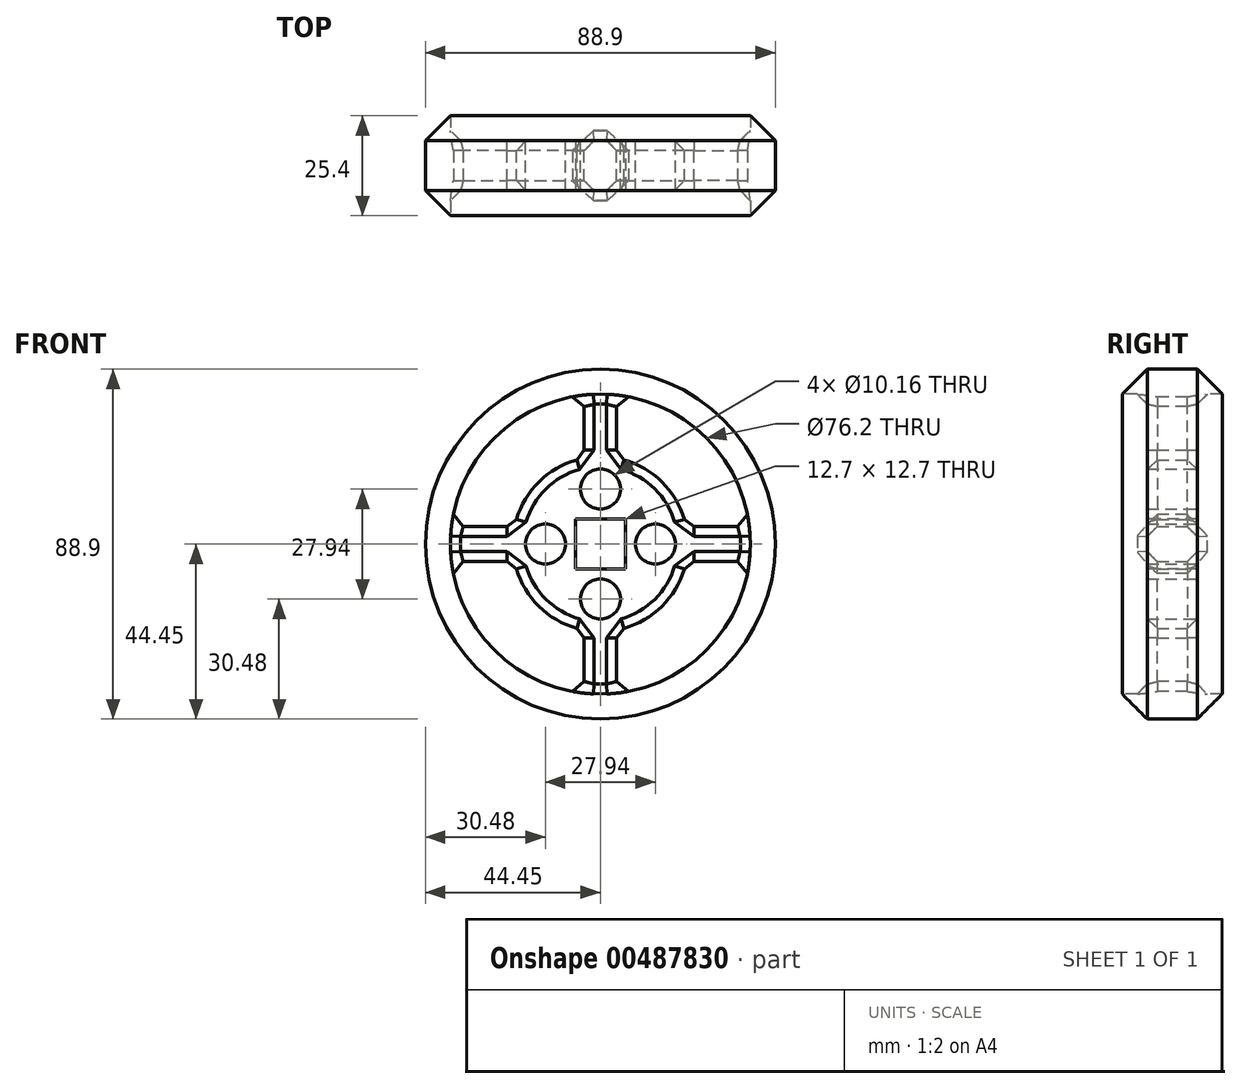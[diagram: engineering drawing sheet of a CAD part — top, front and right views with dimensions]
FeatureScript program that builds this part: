
annotation { "Feature Type Name" : "Feature", "Feature Type Description" : "" }
export const myFeature = defineFeature(function(context is Context, id is Id, definition is map)
    precondition{}
    {
        {
            var Q0;
            Q0=qCreatedBy(makeId("Front.planeOp"),FACE);
            var sketch = newSketch(context, id + "F0", { "sketchPlane" : qUnion([Q0])});
            skCircle(sketch, "E0", {"center": v(0, 0) * mm, "radius": 44.45 * mm});
            skSolve(sketch);
        }
        {
            var Q0;
            Q0=makeQuery(id+"F0.imprint","IMPRINT",FACE,{"disambiguationData":[TD([[makeQuery(id+"F0.imprint","IMPRINT",EDGE,{"derivedFrom":sQuery(id+"F0.wireOp",EDGE,"E0")}),1.0]])]});
            extrude(context, id + "F1", {"entities" : qUnion([Q0]), "depth" : 12.7 * mm});
        }
        {
            var Q0;
            Q0=makeQuery(id+"F1.opExtrude","CAP_FACE",FACE,{"disambiguationData":[OSD([sQuery(id+"F0.wireOp",EDGE,"E0")])],"isStart":false});
            var sketch = newSketch(context, id + "F2", { "sketchPlane" : qUnion([Q0])});
            skCircle(sketch, "E1", {"center": v(0, 0) * mm, "radius": 50.8 * mm});
            skSolve(sketch);
        }
        {
            var Q0;
            Q0=sQuery(id+"F2.wireOp",VERTEX,"E1.center");
            var Q1;
            Q1=makeQuery(id+"F1.opExtrude","SWEPT_BODY",BODY,{"disambiguationData":[OSD([sQuery(id+"F0.wireOp",EDGE,"E0")])]});
            hole(context, id + "F3", {"style" : HoleStyle.SIMPLE, "endStyle" : HoleEndStyle.THROUGH, "holeDiameter" : 76.2 * mm, "isTappedThrough" : true, "tappedDepth" : 12.7 * mm, "tapClearance" : 3, "locations" : qUnion([Q0]), "scope" : qUnion([Q1])});
        }
        {
            var Q0;
            Q0=qCreatedBy(makeId("Front.planeOp"),FACE);
            var sketch = newSketch(context, id + "F4", { "sketchPlane" : qUnion([Q0])});
            skLineSegment(sketch, "E2.bottom", {"start": v(4.13, -42.15) * mm, "end": v(-4.13, -42.15) * mm});
            skLineSegment(sketch, "E2.top", {"start": v(4.13, 42.15) * mm, "end": v(-4.13, 42.15) * mm});
            skLineSegment(sketch, "E2.left", {"start": v(4.13, -42.15) * mm, "end": v(4.13, 42.15) * mm});
            skLineSegment(sketch, "E2.right", {"start": v(-4.13, -42.15) * mm, "end": v(-4.13, 42.15) * mm});
            skPoint(sketch, "E2.middle", {"position": v(0, 0) * mm});
            skLineSegment(sketch, "E3.bottom", {"start": v(42.66, 4.46) * mm, "end": v(-42.66, 4.46) * mm});
            skLineSegment(sketch, "E3.top", {"start": v(42.66, -4.46) * mm, "end": v(-42.66, -4.46) * mm});
            skLineSegment(sketch, "E3.left", {"start": v(42.66, 4.46) * mm, "end": v(42.66, -4.46) * mm});
            skLineSegment(sketch, "E3.right", {"start": v(-42.66, 4.46) * mm, "end": v(-42.66, -4.46) * mm});
            skSolve(sketch);
        }
        {
            var Q0;
            {var subQ5=sQuery(id+"F4.wireOp",EDGE,"E3.left");Q0=makeQuery(id+"F4.imprint","IMPRINT",FACE,{"disambiguationData":[TD([[makeQuery(id+"F4.imprint","IMPRINT",EDGE,{"derivedFrom":subQ5}),-1.0]])]});}
            var Q1;
            {var subQ5=sQuery(id+"F4.wireOp",EDGE,"E3.right");Q1=makeQuery(id+"F4.imprint","IMPRINT",FACE,{"disambiguationData":[TD([[makeQuery(id+"F4.imprint","IMPRINT",EDGE,{"derivedFrom":subQ5}),1.0]])]});}
            var Q2;
            {var subQ0=sQuery(id+"F4.wireOp",EDGE,"E3.top");var subQ1=sQuery(id+"F4.wireOp",EDGE,"E2.left");var subQ2=makeQuery(id+"F4.imprint","INTERSECT",VERTEX,{"derivedFrom":[subQ1,subQ0]});Q2=makeQuery(id+"F4.imprint","IMPRINT",FACE,{"disambiguationData":[TD([[makeQuery(id+"F4.imprint","IMPRINT",EDGE,{"disambiguationData":[TD([[subQ2,-1.0]])],"derivedFrom":subQ1}),1.0]])]});}
            var Q3;
            {var subQ0=sQuery(id+"F4.wireOp",EDGE,"E2.top");Q3=makeQuery(id+"F4.imprint","IMPRINT",FACE,{"disambiguationData":[TD([[makeQuery(id+"F4.imprint","IMPRINT",EDGE,{"derivedFrom":subQ0}),1.0]])]});}
            var Q4;
            {var subQ0=sQuery(id+"F4.wireOp",EDGE,"E2.bottom");Q4=makeQuery(id+"F4.imprint","IMPRINT",FACE,{"disambiguationData":[TD([[makeQuery(id+"F4.imprint","IMPRINT",EDGE,{"derivedFrom":subQ0}),-1.0]])]});}
            extrude(context, id + "F5", {"entities" : qUnion([Q0, Q1, Q2, Q3, Q4]), "operationType" : NewBodyOperationType.ADD, "depth" : 6.35 * mm});
        }
        {
            var Q0;
            Q0=qCreatedBy(makeId("Front.planeOp"),FACE);
            var sketch = newSketch(context, id + "F6", { "sketchPlane" : qUnion([Q0])});
            skCircle(sketch, "E4", {"center": v(0, 0) * mm, "radius": 22.23 * mm});
            skSolve(sketch);
        }
        {
            var Q0;
            Q0=makeQuery(id+"F6.imprint","IMPRINT",FACE,{"disambiguationData":[TD([[makeQuery(id+"F6.imprint","IMPRINT",EDGE,{"derivedFrom":sQuery(id+"F6.wireOp",EDGE,"E4")}),1.0]])]});
            extrude(context, id + "F7", {"entities" : qUnion([Q0]), "operationType" : NewBodyOperationType.ADD, "depth" : 6.35 * mm});
        }
        {
            var Q0;
            Q0=qCreatedBy(makeId("Front.planeOp"),FACE);
            var sketch = newSketch(context, id + "F8", { "sketchPlane" : qUnion([Q0])});
            skCircle(sketch, "E5", {"center": v(0, 13.97) * mm, "radius": 5.08 * mm});
            skCircle(sketch, "E6", {"center": v(13.97, 0) * mm, "radius": 5.08 * mm});
            skCircle(sketch, "E7", {"center": v(0, -13.97) * mm, "radius": 5.08 * mm});
            skCircle(sketch, "E8", {"center": v(-13.97, 0) * mm, "radius": 5.08 * mm});
            skSolve(sketch);
        }
        {
            var Q0;
            Q0=qSketchRegion(id+"F8",true);
            extrude(context, id + "F9", {"entities" : qUnion([Q0]), "operationType" : NewBodyOperationType.REMOVE, "endBound" : BoundingType.THROUGH_ALL, "depth" : 25.4 * mm});
        }
        {
            var Q0;
            Q0=makeQuery(id+"F1.opExtrude","SWEPT_BODY",BODY,{"disambiguationData":[OSD([sQuery(id+"F0.wireOp",EDGE,"E0")])]});
            var Q1;
            Q1=qCreatedBy(makeId("Front.planeOp"),FACE);
            mirror(context, id + "F10", {"operationType" : NewBodyOperationType.ADD, "entities" : qUnion([Q0]), "mirrorPlane" : qUnion([Q1])});
        }
        {
            var Q0;
            {var subQ0=makeQuery(id+"F1.opExtrude","SWEPT_FACE",FACE,{"disambiguationData":[OSD([sQuery(id+"F0.wireOp",EDGE,"E0")])]});Q0=makeQuery(id+"F10.boolean.opBoolean","MERGE",FACE,{"derivedFrom":[subQ0,makeQuery(id+"F10.opPattern","COPY",FACE,{"derivedFrom":subQ0,"instanceName":"1"})]});}
            chamfer(context, id + "F11", {"entities" : qUnion([Q0]), "width" : 6.35 * mm, "tangentPropagation" : true});
        }
        {
            var Q0;
            {var subQ0=sQuery(id+"F4.wireOp",EDGE,"E3.top");var subQ1=makeQuery(id+"F5.opExtrude","SWEPT_FACE",FACE,{"disambiguationData":[OSD([subQ0]),TDD([makeQuery(id+"F4.imprint","IMPRINT",EDGE,{"disambiguationData":[TD([[makeQuery(id+"F4.imprint","INTERSECT",VERTEX,{"derivedFrom":[subQ0,sQuery(id+"F4.wireOp",EDGE,"E3.right")]}),1.0]])],"derivedFrom":subQ0})])]});Q0=makeQuery(id+"F10.boolean.opBoolean","MERGE",FACE,{"derivedFrom":[subQ1,makeQuery(id+"F10.opPattern","COPY",FACE,{"derivedFrom":subQ1,"instanceName":"1"})]});}
            var Q1;
            {var subQ0=sQuery(id+"F4.wireOp",EDGE,"E3.bottom");var subQ1=makeQuery(id+"F5.opExtrude","SWEPT_FACE",FACE,{"disambiguationData":[OSD([subQ0]),TDD([makeQuery(id+"F4.imprint","IMPRINT",EDGE,{"disambiguationData":[TD([[makeQuery(id+"F4.imprint","INTERSECT",VERTEX,{"derivedFrom":[subQ0,sQuery(id+"F4.wireOp",EDGE,"E3.right")]}),1.0]])],"derivedFrom":subQ0})])]});Q1=makeQuery(id+"F10.boolean.opBoolean","MERGE",FACE,{"derivedFrom":[subQ1,makeQuery(id+"F10.opPattern","COPY",FACE,{"derivedFrom":subQ1,"instanceName":"1"})]});}
            var Q2;
            {var subQ0=sQuery(id+"F4.wireOp",EDGE,"E2.right");var subQ1=makeQuery(id+"F5.opExtrude","SWEPT_FACE",FACE,{"disambiguationData":[OSD([subQ0]),TDD([makeQuery(id+"F4.imprint","IMPRINT",EDGE,{"disambiguationData":[TD([[makeQuery(id+"F4.imprint","INTERSECT",VERTEX,{"derivedFrom":[sQuery(id+"F4.wireOp",EDGE,"E2.top"),subQ0]}),1.0]])],"derivedFrom":subQ0})])]});Q2=makeQuery(id+"F10.boolean.opBoolean","MERGE",FACE,{"derivedFrom":[subQ1,makeQuery(id+"F10.opPattern","COPY",FACE,{"derivedFrom":subQ1,"instanceName":"1"})]});}
            var Q3;
            {var subQ0=sQuery(id+"F4.wireOp",EDGE,"E2.left");var subQ1=makeQuery(id+"F5.opExtrude","SWEPT_FACE",FACE,{"disambiguationData":[OSD([subQ0]),TDD([makeQuery(id+"F4.imprint","IMPRINT",EDGE,{"disambiguationData":[TD([[makeQuery(id+"F4.imprint","INTERSECT",VERTEX,{"derivedFrom":[sQuery(id+"F4.wireOp",EDGE,"E2.top"),subQ0]}),1.0]])],"derivedFrom":subQ0})])]});Q3=makeQuery(id+"F10.boolean.opBoolean","MERGE",FACE,{"derivedFrom":[subQ1,makeQuery(id+"F10.opPattern","COPY",FACE,{"derivedFrom":subQ1,"instanceName":"1"})]});}
            var Q4;
            {var subQ0=sQuery(id+"F4.wireOp",EDGE,"E3.bottom");var subQ1=makeQuery(id+"F5.opExtrude","SWEPT_FACE",FACE,{"disambiguationData":[OSD([subQ0]),TDD([makeQuery(id+"F4.imprint","IMPRINT",EDGE,{"disambiguationData":[TD([[makeQuery(id+"F4.imprint","INTERSECT",VERTEX,{"derivedFrom":[subQ0,sQuery(id+"F4.wireOp",EDGE,"E3.left")]}),-1.0]])],"derivedFrom":subQ0})])]});Q4=makeQuery(id+"F10.boolean.opBoolean","MERGE",FACE,{"derivedFrom":[subQ1,makeQuery(id+"F10.opPattern","COPY",FACE,{"derivedFrom":subQ1,"instanceName":"1"})]});}
            var Q5;
            {var subQ0=sQuery(id+"F4.wireOp",EDGE,"E3.top");var subQ1=makeQuery(id+"F5.opExtrude","SWEPT_FACE",FACE,{"disambiguationData":[OSD([subQ0]),TDD([makeQuery(id+"F4.imprint","IMPRINT",EDGE,{"disambiguationData":[TD([[makeQuery(id+"F4.imprint","INTERSECT",VERTEX,{"derivedFrom":[subQ0,sQuery(id+"F4.wireOp",EDGE,"E3.left")]}),-1.0]])],"derivedFrom":subQ0})])]});Q5=makeQuery(id+"F10.boolean.opBoolean","MERGE",FACE,{"derivedFrom":[subQ1,makeQuery(id+"F10.opPattern","COPY",FACE,{"derivedFrom":subQ1,"instanceName":"1"})]});}
            var Q6;
            {var subQ0=sQuery(id+"F4.wireOp",EDGE,"E2.left");var subQ1=makeQuery(id+"F5.opExtrude","SWEPT_FACE",FACE,{"disambiguationData":[OSD([subQ0]),TDD([makeQuery(id+"F4.imprint","IMPRINT",EDGE,{"disambiguationData":[TD([[makeQuery(id+"F4.imprint","INTERSECT",VERTEX,{"derivedFrom":[sQuery(id+"F4.wireOp",EDGE,"E2.bottom"),subQ0]}),-1.0]])],"derivedFrom":subQ0})])]});Q6=makeQuery(id+"F10.boolean.opBoolean","MERGE",FACE,{"derivedFrom":[subQ1,makeQuery(id+"F10.opPattern","COPY",FACE,{"derivedFrom":subQ1,"instanceName":"1"})]});}
            var Q7;
            {var subQ0=sQuery(id+"F4.wireOp",EDGE,"E2.right");var subQ1=makeQuery(id+"F5.opExtrude","SWEPT_FACE",FACE,{"disambiguationData":[OSD([subQ0]),TDD([makeQuery(id+"F4.imprint","IMPRINT",EDGE,{"disambiguationData":[TD([[makeQuery(id+"F4.imprint","INTERSECT",VERTEX,{"derivedFrom":[sQuery(id+"F4.wireOp",EDGE,"E2.bottom"),subQ0]}),-1.0]])],"derivedFrom":subQ0})])]});Q7=makeQuery(id+"F10.boolean.opBoolean","MERGE",FACE,{"derivedFrom":[subQ1,makeQuery(id+"F10.opPattern","COPY",FACE,{"derivedFrom":subQ1,"instanceName":"1"})]});}
            var Q8;
            {var subQ4=sQuery(id+"F4.wireOp",EDGE,"E2.right");var subQ7=sQuery(id+"F4.wireOp",EDGE,"E2.bottom");var subQ9=sQuery(id+"F6.wireOp",EDGE,"E4");var subQ10=makeQuery(id+"F7.boolean.opBoolean","SPLIT",FACE,{"disambiguationData":[TD([makeQuery(id+"F5.opExtrude","SWEPT_FACE",FACE,{"disambiguationData":[OSD([subQ4]),TDD([makeQuery(id+"F4.imprint","IMPRINT",EDGE,{"disambiguationData":[TD([[makeQuery(id+"F4.imprint","INTERSECT",VERTEX,{"derivedFrom":[subQ7,subQ4]}),-1.0]])],"derivedFrom":subQ4})])]})])],"derivedFrom":makeQuery(id+"F7.opExtrude","SWEPT_FACE",FACE,{"disambiguationData":[OSD([subQ9])]})});Q8=makeQuery(id+"F10.boolean.opBoolean","MERGE",FACE,{"derivedFrom":[subQ10,makeQuery(id+"F10.opPattern","COPY",FACE,{"derivedFrom":subQ10,"instanceName":"1"})]});}
            var Q9;
            {var subQ0=sQuery(id+"F4.wireOp",EDGE,"E2.right");var subQ1=sQuery(id+"F4.wireOp",EDGE,"E2.top");var subQ4=sQuery(id+"F6.wireOp",EDGE,"E4");var subQ10=makeQuery(id+"F7.boolean.opBoolean","SPLIT",FACE,{"disambiguationData":[TD([makeQuery(id+"F5.opExtrude","SWEPT_FACE",FACE,{"disambiguationData":[OSD([subQ0]),TDD([makeQuery(id+"F4.imprint","IMPRINT",EDGE,{"disambiguationData":[TD([[makeQuery(id+"F4.imprint","INTERSECT",VERTEX,{"derivedFrom":[subQ1,subQ0]}),1.0]])],"derivedFrom":subQ0})])]})])],"derivedFrom":makeQuery(id+"F7.opExtrude","SWEPT_FACE",FACE,{"disambiguationData":[OSD([subQ4])]})});Q9=makeQuery(id+"F10.boolean.opBoolean","MERGE",FACE,{"derivedFrom":[subQ10,makeQuery(id+"F10.opPattern","COPY",FACE,{"derivedFrom":subQ10,"instanceName":"1"})]});}
            var Q10;
            {var subQ0=sQuery(id+"F4.wireOp",EDGE,"E2.left");var subQ1=sQuery(id+"F4.wireOp",EDGE,"E2.top");var subQ9=sQuery(id+"F6.wireOp",EDGE,"E4");var subQ10=makeQuery(id+"F7.boolean.opBoolean","SPLIT",FACE,{"disambiguationData":[TD([makeQuery(id+"F5.opExtrude","SWEPT_FACE",FACE,{"disambiguationData":[OSD([subQ0]),TDD([makeQuery(id+"F4.imprint","IMPRINT",EDGE,{"disambiguationData":[TD([[makeQuery(id+"F4.imprint","INTERSECT",VERTEX,{"derivedFrom":[subQ1,subQ0]}),1.0]])],"derivedFrom":subQ0})])]})])],"derivedFrom":makeQuery(id+"F7.opExtrude","SWEPT_FACE",FACE,{"disambiguationData":[OSD([subQ9])]})});Q10=makeQuery(id+"F10.boolean.opBoolean","MERGE",FACE,{"derivedFrom":[subQ10,makeQuery(id+"F10.opPattern","COPY",FACE,{"derivedFrom":subQ10,"instanceName":"1"})]});}
            var Q11;
            {var subQ0=sQuery(id+"F4.wireOp",EDGE,"E2.left");var subQ1=sQuery(id+"F4.wireOp",EDGE,"E2.bottom");var subQ9=sQuery(id+"F6.wireOp",EDGE,"E4");var subQ10=makeQuery(id+"F7.boolean.opBoolean","SPLIT",FACE,{"disambiguationData":[TD([makeQuery(id+"F5.opExtrude","SWEPT_FACE",FACE,{"disambiguationData":[OSD([subQ0]),TDD([makeQuery(id+"F4.imprint","IMPRINT",EDGE,{"disambiguationData":[TD([[makeQuery(id+"F4.imprint","INTERSECT",VERTEX,{"derivedFrom":[subQ1,subQ0]}),-1.0]])],"derivedFrom":subQ0})])]})])],"derivedFrom":makeQuery(id+"F7.opExtrude","SWEPT_FACE",FACE,{"disambiguationData":[OSD([subQ9])]})});Q11=makeQuery(id+"F10.boolean.opBoolean","MERGE",FACE,{"derivedFrom":[subQ10,makeQuery(id+"F10.opPattern","COPY",FACE,{"derivedFrom":subQ10,"instanceName":"1"})]});}
            chamfer(context, id + "F12", {"entities" : qUnion([Q0, Q1, Q2, Q3, Q4, Q5, Q6, Q7, Q8, Q9, Q10, Q11]), "width" : 2.54 * mm, "tangentPropagation" : true});
        }
        {
            var Q0;
            Q0=makeQuery(id+"F7.boolean.opBoolean","MERGE",FACE,{"derivedFrom":[makeQuery(id+"F5.opExtrude","CAP_FACE",FACE,{"disambiguationData":[OSD([sQuery(id+"F4.wireOp",EDGE,"E2.bottom"),sQuery(id+"F4.wireOp",EDGE,"E2.top"),sQuery(id+"F4.wireOp",EDGE,"E2.left"),sQuery(id+"F4.wireOp",EDGE,"E2.right"),sQuery(id+"F4.wireOp",EDGE,"E3.bottom"),sQuery(id+"F4.wireOp",EDGE,"E3.top"),sQuery(id+"F4.wireOp",EDGE,"E3.left"),sQuery(id+"F4.wireOp",EDGE,"E3.right")])],"isStart":false}),makeQuery(id+"F7.opExtrude","CAP_FACE",FACE,{"disambiguationData":[OSD([sQuery(id+"F6.wireOp",EDGE,"E4")])],"isStart":false})]});
            var sketch = newSketch(context, id + "F13", { "sketchPlane" : qUnion([Q0])});
            skLineSegment(sketch, "E9.bottom", {"start": v(6.35, -6.35) * mm, "end": v(-6.35, -6.35) * mm});
            skLineSegment(sketch, "E9.top", {"start": v(6.35, 6.35) * mm, "end": v(-6.35, 6.35) * mm});
            skLineSegment(sketch, "E9.left", {"start": v(6.35, -6.35) * mm, "end": v(6.35, 6.35) * mm});
            skLineSegment(sketch, "E9.right", {"start": v(-6.35, -6.35) * mm, "end": v(-6.35, 6.35) * mm});
            skPoint(sketch, "E9.middle", {"position": v(0, 0) * mm});
            skSolve(sketch);
        }
        {
            var Q0;
            Q0 = qSketchRegion(id + "F13", true);
            extrude(context, id + "F14", {"entities" : qUnion([Q0]), "operationType" : NewBodyOperationType.REMOVE, "endBound" : BoundingType.THROUGH_ALL, "oppositeDirection" : true, "depth" : 25.4 * mm});
        }
    });
